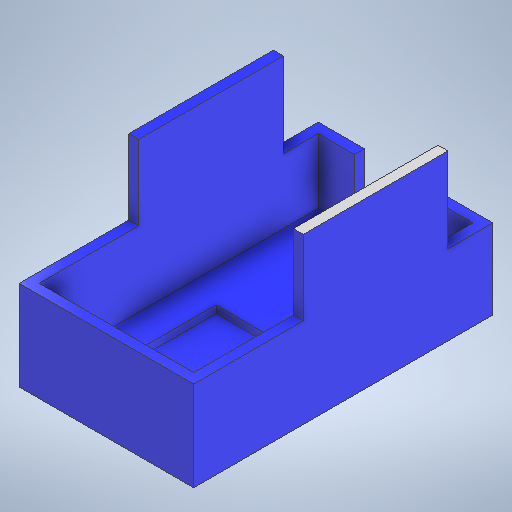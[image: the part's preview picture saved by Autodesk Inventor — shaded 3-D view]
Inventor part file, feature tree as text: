
AUTODESK INVENTOR PART (.ipt)
format: ipt  version: 2025.1 (Build 291241020, 241B)  size: 305,152 bytes
history: native  units: in
note: dims shown in document units (in); Inventor stores cm internally (conversion verified against a paired STEP export)
features: sketch x7, extrude x6, projected_geometry x3
ambient origin geometry x8: Origin, YZ Plane, XZ Plane, XY Plane, X Axis, Y Axis, Z Axis, Center Point
bodies: Solid1 (feature_tree)
feature tree (16):
  extrude  "Extrusion1"  Depth=2.2047in
  extrude  "Extrusion2"  Depth=0.7087in
  extrude  "Extrusion3"  Depth=0.2559in
  extrude  "Extrusion4"  Depth=0.0591in TaperAngle=0.0deg
  extrude  "Extrusion5"  Depth=1.1811in TaperAngle=0.0deg
  sketch  "Sketch8"  dims[d20=0.3543in d21=0.6693in d22=0.0in d23=0.0787in d26=0.0787in d29=0.6496in d32=1.5551in d33=1.125in d34=0.0in]
  extrude  "Extrusion6"  Depth=0.5906in TaperAngle=0.0deg
  sketch  "Sketch1"  dims[d0=1.2205in d1=2.2047in]
  sketch  "Sketch2"  dims[d2=0.1181in d3=0.0in d4=0.7087in]
  projected_geometry  "Projected Loop1"
  sketch  "Sketch3"  dims[d5=0.748in d8=0.2559in]
  projected_geometry  "Projected Loop2"
  sketch  "Sketch4"  dims[d9=0.374in d10=0.0591in d11=0.0in]
  projected_geometry  "Projected Loop3"
  sketch  "Sketch6"  dims[d12=0.0787in d13=1.1811in d14=0.1181in d15=0.0in d16=0.0in]
  sketch  "Sketch7"  dims[d17=0.8661in d18=0.5906in d19=0.0in]
